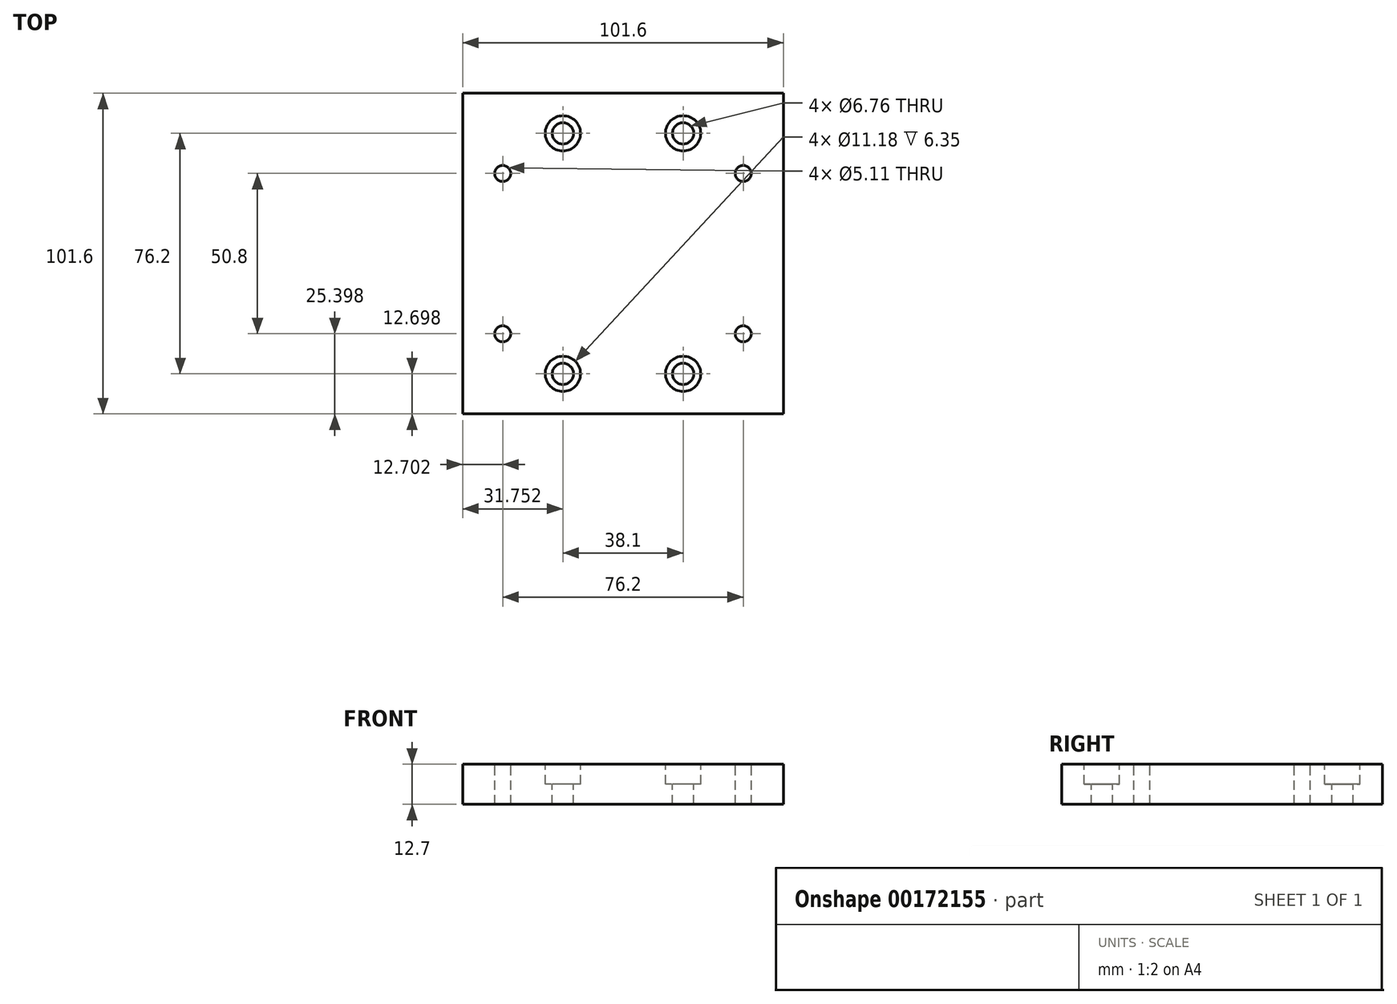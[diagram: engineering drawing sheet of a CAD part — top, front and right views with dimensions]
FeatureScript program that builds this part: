
annotation { "Feature Type Name" : "Feature", "Feature Type Description" : "" }
export const myFeature = defineFeature(function(context is Context, id is Id, definition is map)
    precondition{}
    {
        {
            var Q0;
            Q0=qCreatedBy(makeId("Top.planeOp"),FACE);
            var sketch = newSketch(context, id + "F0", { "sketchPlane" : qUnion([Q0])});
            skLineSegment(sketch, "E0.bottom", {"start": v(-51.09, -63.51) * mm, "end": v(50.51, -63.51) * mm});
            skLineSegment(sketch, "E0.top", {"start": v(-51.09, 38.09) * mm, "end": v(50.51, 38.09) * mm});
            skLineSegment(sketch, "E0.left", {"start": v(-51.09, -63.51) * mm, "end": v(-51.09, 38.09) * mm});
            skLineSegment(sketch, "E0.right", {"start": v(50.51, -63.51) * mm, "end": v(50.51, 38.09) * mm});
            skSolve(sketch);
        }
        {
            var Q0;
            Q0=makeQuery(id+"F0.imprint","IMPRINT",FACE,{"disambiguationData":[TD([[makeQuery(id+"F0.imprint","IMPRINT",EDGE,{"derivedFrom":sQuery(id+"F0.wireOp",EDGE,"E0.bottom")}),1.0]])]});
            extrude(context, id + "F1", {"entities" : qUnion([Q0]), "depth" : 12.7 * mm});
        }
        {
            var Q0;
            Q0=makeQuery(id+"F1.opExtrude","CAP_FACE",FACE,{"disambiguationData":[OSD([sQuery(id+"F0.wireOp",EDGE,"E0.bottom"),sQuery(id+"F0.wireOp",EDGE,"E0.top"),sQuery(id+"F0.wireOp",EDGE,"E0.left"),sQuery(id+"F0.wireOp",EDGE,"E0.right")])],"isStart":false});
            var sketch = newSketch(context, id + "F2", { "sketchPlane" : qUnion([Q0])});
            skCircle(sketch, "E1", {"center": v(-19.34, 25.39) * mm, "radius": 3.38 * mm});
            skCircle(sketch, "E2", {"center": v(18.76, 25.39) * mm, "radius": 3.38 * mm});
            skPoint(sketch, "E3", {"position": v(-19.34, -50.81) * mm});
            skPoint(sketch, "E4", {"position": v(18.76, -50.81) * mm});
            skSolve(sketch);
        }
        {
            var Q0;
            Q0=sQuery(id+"F2.wireOp",VERTEX,"E1.center");
            var Q1;
            Q1=sQuery(id+"F2.wireOp",VERTEX,"E2.center");
            var Q2;
            Q2=sQuery(id+"F2.wireOp",VERTEX,"E3");
            var Q3;
            Q3=sQuery(id+"F2.wireOp",VERTEX,"E4");
            var Q4;
            Q4=makeQuery(id+"F1.opExtrude","SWEPT_BODY",BODY,{"disambiguationData":[OSD([sQuery(id+"F0.wireOp",EDGE,"E0.bottom"),sQuery(id+"F0.wireOp",EDGE,"E0.top"),sQuery(id+"F0.wireOp",EDGE,"E0.left"),sQuery(id+"F0.wireOp",EDGE,"E0.right")])]});
            hole(context, id + "F3", {"style" : HoleStyle.C_BORE, "endStyle" : HoleEndStyle.THROUGH, "holeDiameter" : 6.76 * mm, "cBoreDiameter" : 11.18 * mm, "cBoreDepth" : 6.35 * mm, "locations" : qUnion([Q0, Q1, Q2, Q3]), "scope" : qUnion([Q4]), "isTappedThrough" : true});
        }
        {
            var Q0;
            Q0=makeQuery(id+"F1.opExtrude","CAP_FACE",FACE,{"disambiguationData":[OSD([sQuery(id+"F0.wireOp",EDGE,"E0.bottom"),sQuery(id+"F0.wireOp",EDGE,"E0.top"),sQuery(id+"F0.wireOp",EDGE,"E0.left"),sQuery(id+"F0.wireOp",EDGE,"E0.right")])],"isStart":false});
            var sketch = newSketch(context, id + "F4", { "sketchPlane" : qUnion([Q0])});
            skPoint(sketch, "E5", {"position": v(-38.39, 12.69) * mm});
            skPoint(sketch, "E6", {"position": v(-38.39, -38.11) * mm});
            skPoint(sketch, "E7", {"position": v(37.81, 12.69) * mm});
            skPoint(sketch, "E8", {"position": v(37.81, -38.11) * mm});
            skSolve(sketch);
        }
        {
            var Q0;
            Q0=sQuery(id+"F4.wireOp",VERTEX,"E5");
            var Q1;
            Q1=sQuery(id+"F4.wireOp",VERTEX,"E6");
            var Q2;
            Q2=sQuery(id+"F4.wireOp",VERTEX,"E8");
            var Q3;
            Q3=sQuery(id+"F4.wireOp",VERTEX,"E7");
            var Q4;
            Q4=makeQuery(id+"F1.opExtrude","SWEPT_BODY",BODY,{"disambiguationData":[OSD([sQuery(id+"F0.wireOp",EDGE,"E0.bottom"),sQuery(id+"F0.wireOp",EDGE,"E0.top"),sQuery(id+"F0.wireOp",EDGE,"E0.left"),sQuery(id+"F0.wireOp",EDGE,"E0.right")])]});
            hole(context, id + "F5", {"style" : HoleStyle.SIMPLE, "endStyle" : HoleEndStyle.THROUGH, "holeDiameter" : 5.1 * mm, "locations" : qUnion([Q0, Q1, Q2, Q3]), "scope" : qUnion([Q4]), "isTappedThrough" : true});
        }
    });
